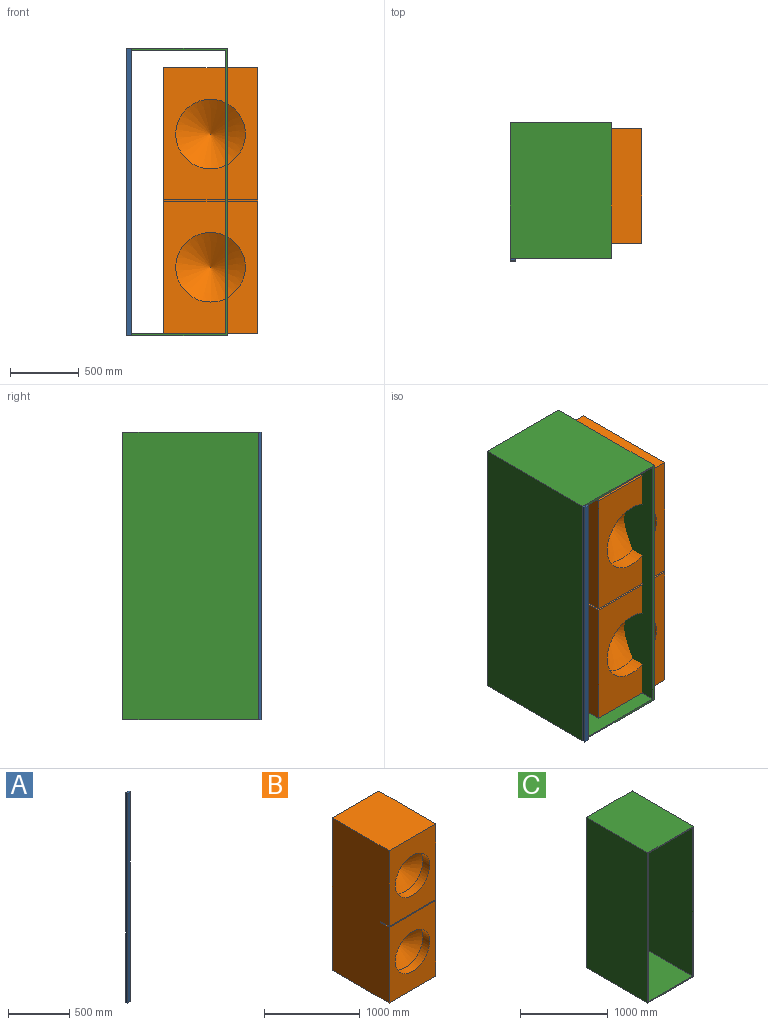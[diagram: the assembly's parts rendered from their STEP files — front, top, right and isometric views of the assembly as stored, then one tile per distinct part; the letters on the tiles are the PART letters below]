
ASSEMBLY  parts=3 mates=4
PART A: 6 faces, bbox 38.1x19.1x2095.5 mm
  f0: plane 2095.5x19.05mm, normal (-1,0,0), area 39919.3mm2, adj f1,f3,f4,f5
  f1: plane 2095.5x38.1mm, normal (0,-1,0), area 79838.6mm2, adj f0,f2,f4,f5
  f2: plane 2095.5x19.05mm, normal (1,0,0), area 39919.3mm2, adj f1,f3,f4,f5
  f3: plane 2095.5x38.1mm, normal (0,1,0), area 79838.6mm2, adj f0,f2,f4,f5
  f4: plane 38.1x19.05mm, normal (0,0,1), area 725.8mm2, adj f0,f1,f2,f3
  f5: plane 38.1x19.05mm, normal (0,0,-1), area 725.8mm2, adj f0,f1,f2,f3
PART B: 14 faces, bbox 685.8x838.2x1943.1 mm
  f0: plane 965.2x685.8mm, normal (0,-1,0), area 459251.2mm2, adj f1,f3,f6,f8,f12
  f1: plane 1943.1x838.2mm, normal (1,0,0), area 1627093.5mm2, adj f0,f2,f4,f5,f6,f11,f12,f13
  f2: plane 1943.1x685.8mm, normal (0,1,0), area 1332578mm2, adj f1,f3,f5,f6
  f3: plane 1943.1x838.2mm, normal (-1,0,0), area 1627093.5mm2, adj f0,f2,f4,f5,f6,f11,f12,f13
  f4: plane 965.2x685.8mm, normal (0,-1,0), area 459251.2mm2, adj f1,f3,f5,f10,f11
  f5: plane 838.2x685.8mm, normal (0,0,1), area 574837.6mm2, adj f1,f2,f3,f4
  f6: plane 838.2x685.8mm, normal (0,0,-1), area 574837.6mm2, adj f0,f1,f2,f3
  f7: cone r=0mm half-angle=59deg, axis (0,-1,0), area 236456.7mm2, adj f8
  f8: cylinder r=254mm len=508mm, axis (0,-1,0), area 162146.4mm2, adj f0,f7
  f9: cone r=0mm half-angle=59deg, axis (0,-1,0), area 236456.7mm2, adj f10
  f10: cylinder r=254mm len=508mm, axis (0,-1,0), area 162146.4mm2, adj f4,f9
  f11: plane 685.8x127mm, normal (0,0,-1), area 87096.6mm2, adj f1,f3,f4,f13
  f12: plane 685.8x127mm, normal (0,0,1), area 87096.6mm2, adj f0,f1,f3,f13
  f13: plane 685.8x12.7mm, normal (0,-1,0), area 8709.7mm2, adj f1,f3,f11,f12
PART C: 10 faces, bbox 736.6x989x2095.5 mm
  f0: plane 2095.5x736.6mm, normal (0,-1,0), area 71290.2mm2, adj f1,f2,f3,f4,f6,f7,f8,f9
  f1: plane 2095.5x989.01mm, normal (-1,0,0), area 2072475.7mm2, adj f0,f2,f4,f5
  f2: plane 989.01x736.6mm, normal (0,0,-1), area 728506.6mm2, adj f0,f1,f3,f5
  f3: plane 2095.5x989.01mm, normal (1,0,0), area 2072475.7mm2, adj f0,f2,f4,f5
  f4: plane 989.01x736.6mm, normal (0,0,1), area 728506.6mm2, adj f0,f1,f3,f5
  f5: plane 2095.5x736.6mm, normal (0,1,0), area 71290.2mm2, adj f1,f2,f3,f4,f6,f7,f8,f9
  f6: plane 2070.1x989.01mm, normal (1,0,0), area 2047354.8mm2, adj f0,f5,f7,f9
  f7: plane 989.01x711.2mm, normal (0,0,1), area 703385.7mm2, adj f0,f5,f6,f8
  f8: plane 2070.1x989.01mm, normal (-1,0,0), area 2047354.8mm2, adj f0,f5,f7,f9
  f9: plane 989.01x711.2mm, normal (0,0,-1), area 703385.7mm2, adj f0,f5,f6,f8
PLACE A rot(axis=(0,0,-1),180deg) t=(-845.09,-2583.18,-185.43)mm
PLACE B t=(-269.67,-2055.5,-172.73)mm
PLACE C t=(-883.19,-1594.17,-185.43)mm
MATE planar A.f2 <-> C.f1  axis (-1,0,0) through (-883.19,-2592.71,862.32)mm
MATE planar A.f4 <-> C.f4  axis (0,0,1) through (-883.19,-2583.18,1910.07)mm
MATE planar B.f6 <-> C.f7  axis (0,0,-1) through (-269.67,-2055.5,-172.73)mm
MATE planar A.f1 <-> C.f0  axis (0,1,0) through (-864.14,-2583.18,862.32)mm
